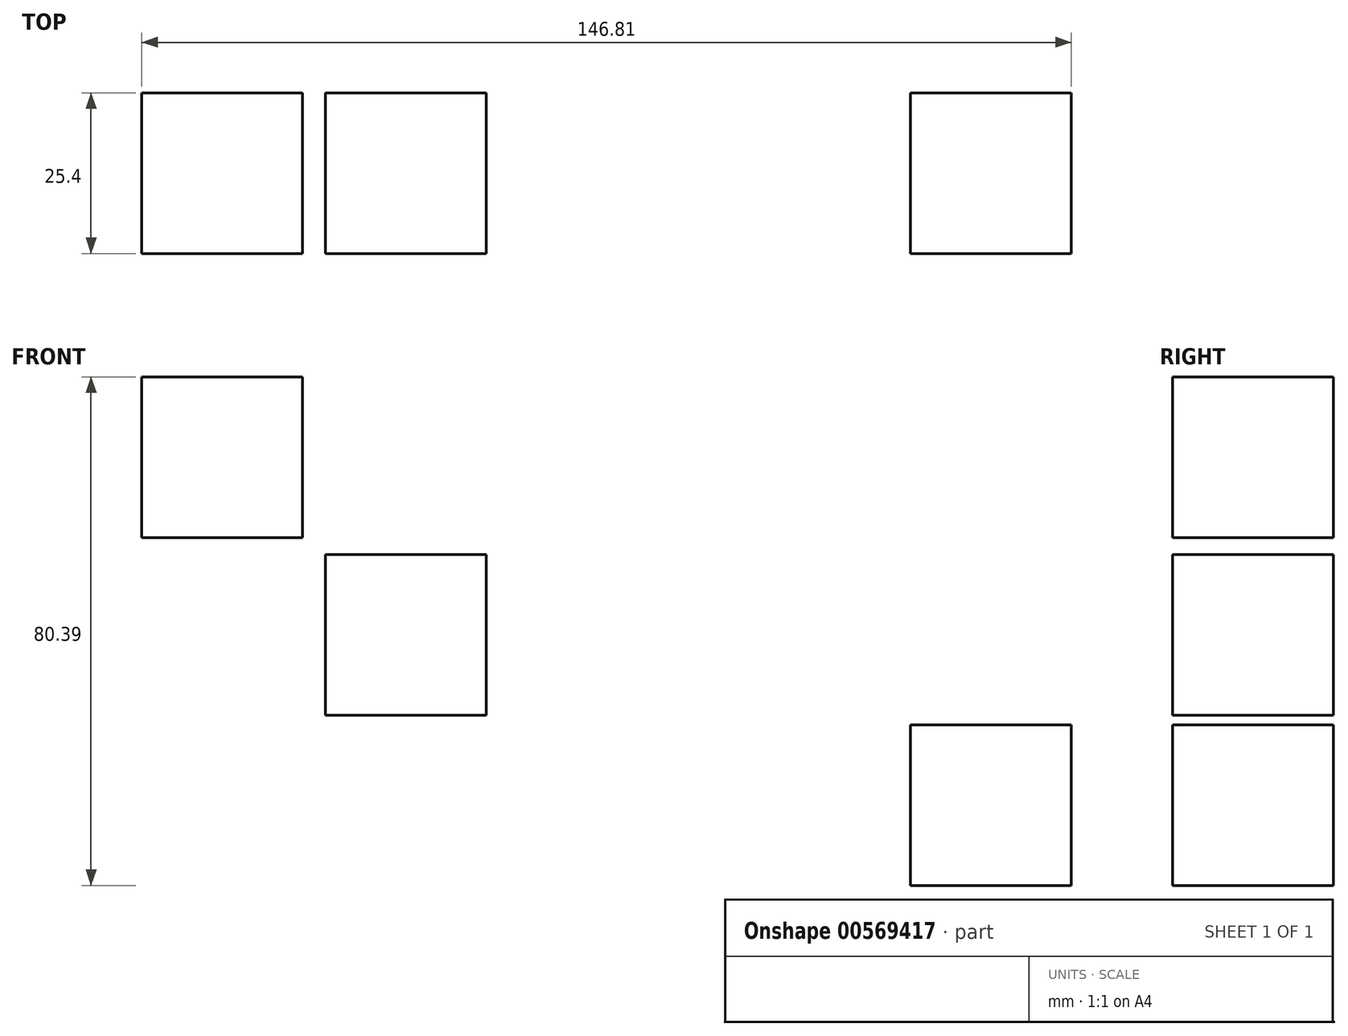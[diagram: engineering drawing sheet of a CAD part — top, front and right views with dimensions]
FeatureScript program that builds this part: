
annotation { "Feature Type Name" : "Feature", "Feature Type Description" : "" }
export const myFeature = defineFeature(function(context is Context, id is Id, definition is map)
    precondition{}
    {
        {
            var Q0;
            Q0=qCreatedBy(makeId("Front.planeOp"),FACE);
            var sketch = newSketch(context, id + "F0", { "sketchPlane" : qUnion([Q0])});
            skLineSegment(sketch, "E0.bottom", {"start": v(-85.78, 32.32) * mm, "end": v(-60.38, 32.32) * mm});
            skLineSegment(sketch, "E0.top", {"start": v(-85.78, 6.92) * mm, "end": v(-60.38, 6.92) * mm});
            skLineSegment(sketch, "E0.left", {"start": v(-85.78, 32.32) * mm, "end": v(-85.78, 6.92) * mm});
            skLineSegment(sketch, "E0.right", {"start": v(-60.38, 32.32) * mm, "end": v(-60.38, 6.92) * mm});
            skSolve(sketch);
        }
        {
            var Q0;
            Q0=makeQuery(id+"F0.imprint","IMPRINT",FACE,{"disambiguationData":[TD([[makeQuery(id+"F0.imprint","IMPRINT",EDGE,{"derivedFrom":sQuery(id+"F0.wireOp",EDGE,"E0.bottom")}),-1.0]])]});
            extrude(context, id + "F1", {"entities" : qUnion([Q0]), "depth" : 25.4 * mm, "offsetDistance" : 25.4 * mm});
        }
        {
            var Q0;
            Q0=qCreatedBy(makeId("Front.planeOp"),FACE);
            var sketch = newSketch(context, id + "F2", { "sketchPlane" : qUnion([Q0])});
            skLineSegment(sketch, "E1.bottom", {"start": v(6.63, 5.45) * mm, "end": v(32.03, 5.45) * mm});
            skLineSegment(sketch, "E1.top", {"start": v(6.63, -19.95) * mm, "end": v(32.03, -19.95) * mm});
            skLineSegment(sketch, "E1.left", {"start": v(6.63, 5.45) * mm, "end": v(6.63, -19.95) * mm});
            skLineSegment(sketch, "E1.right", {"start": v(32.03, 5.45) * mm, "end": v(32.03, -19.95) * mm});
            skSolve(sketch);
        }
        {
            var Q0;
            Q0 = qSketchRegion(id + "F2", true);
            extrude(context, id + "F3", {"entities" : qUnion([Q0]), "depth" : 25.4 * mm, "offsetDistance" : 25.4 * mm});
        }
        {
            var Q0;
            Q0=qCreatedBy(makeId("Front.planeOp"),FACE);
            var sketch = newSketch(context, id + "F4", { "sketchPlane" : qUnion([Q0])});
            skLineSegment(sketch, "E2.bottom", {"start": v(-114.78, 60.44) * mm, "end": v(-89.38, 60.44) * mm});
            skLineSegment(sketch, "E2.top", {"start": v(-114.78, 35.04) * mm, "end": v(-89.38, 35.04) * mm});
            skLineSegment(sketch, "E2.left", {"start": v(-114.78, 60.44) * mm, "end": v(-114.78, 35.04) * mm});
            skLineSegment(sketch, "E2.right", {"start": v(-89.38, 60.44) * mm, "end": v(-89.38, 35.04) * mm});
            skSolve(sketch);
        }
        {
            var Q0;
            Q0=makeQuery(id+"F4.imprint","IMPRINT",FACE,{"disambiguationData":[TD([[makeQuery(id+"F4.imprint","IMPRINT",EDGE,{"derivedFrom":sQuery(id+"F4.wireOp",EDGE,"E2.bottom")}),-1.0]])]});
            extrude(context, id + "F5", {"entities" : qUnion([Q0]), "depth" : 25.4 * mm, "offsetDistance" : 25.4 * mm});
        }
    });
